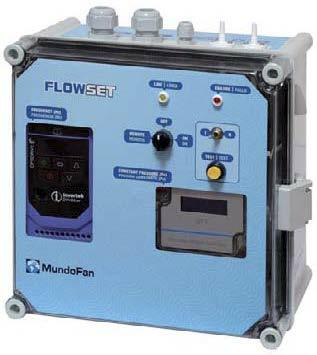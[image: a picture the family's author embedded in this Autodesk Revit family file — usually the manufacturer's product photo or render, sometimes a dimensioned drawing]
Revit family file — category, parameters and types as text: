
# Revit family: FLOWSET-075_VE10840
name_source: partatom
category: Aparatos eléctricos
revit_build: Autodesk Revit 2016 (Build: 20150220_1215(x64)
units: mm (PartAtom-declared; Revit-internal decimal feet)

## family parameters
Compartido = No
Corte con vacíos al cargar = No
Cota de conector redondo = Diámetro de uso
Mantener orientación de anotación = No
Número OmniClass = 23.80.00.00
Punto de cálculo de habitación = No
Se basa en plano de trabajo = No
Siempre vertical = Sí
Tipo de pieza = Caja de conexiones
Título OmniClass = Electric Power and Lighting

## types (1)
- FLOWSET
    Alimentación = 230Vac monofásico
    Corriente = 7 A
    Costo = 0 $
    Código de montaje = VE10840
    Descripción = CONTROL EFICIENCIA ENERGETICA PARA VENTILADORES - Caudal aire constante
    Dimensiones máx. = 270x300x170 mm
    Fabricante = SALVADOR ESCODA
    Imagen de tipo = flowset.jpg
    Leds = linea / fallo
    Modelo = FLOWSET 0,75kW
    Normativas = EN-ISO 14644-1:2000
    Potencia = 0,75 kW
    Regulación = Mediante sonda analógica de presión
    Salida = 230Vac monofásico
    Selector = 3 posiciones remoto / off / on
    URL = www.salvadorescoda.com
    Visualización = frecuencia (Hz) y presión (Pa)
